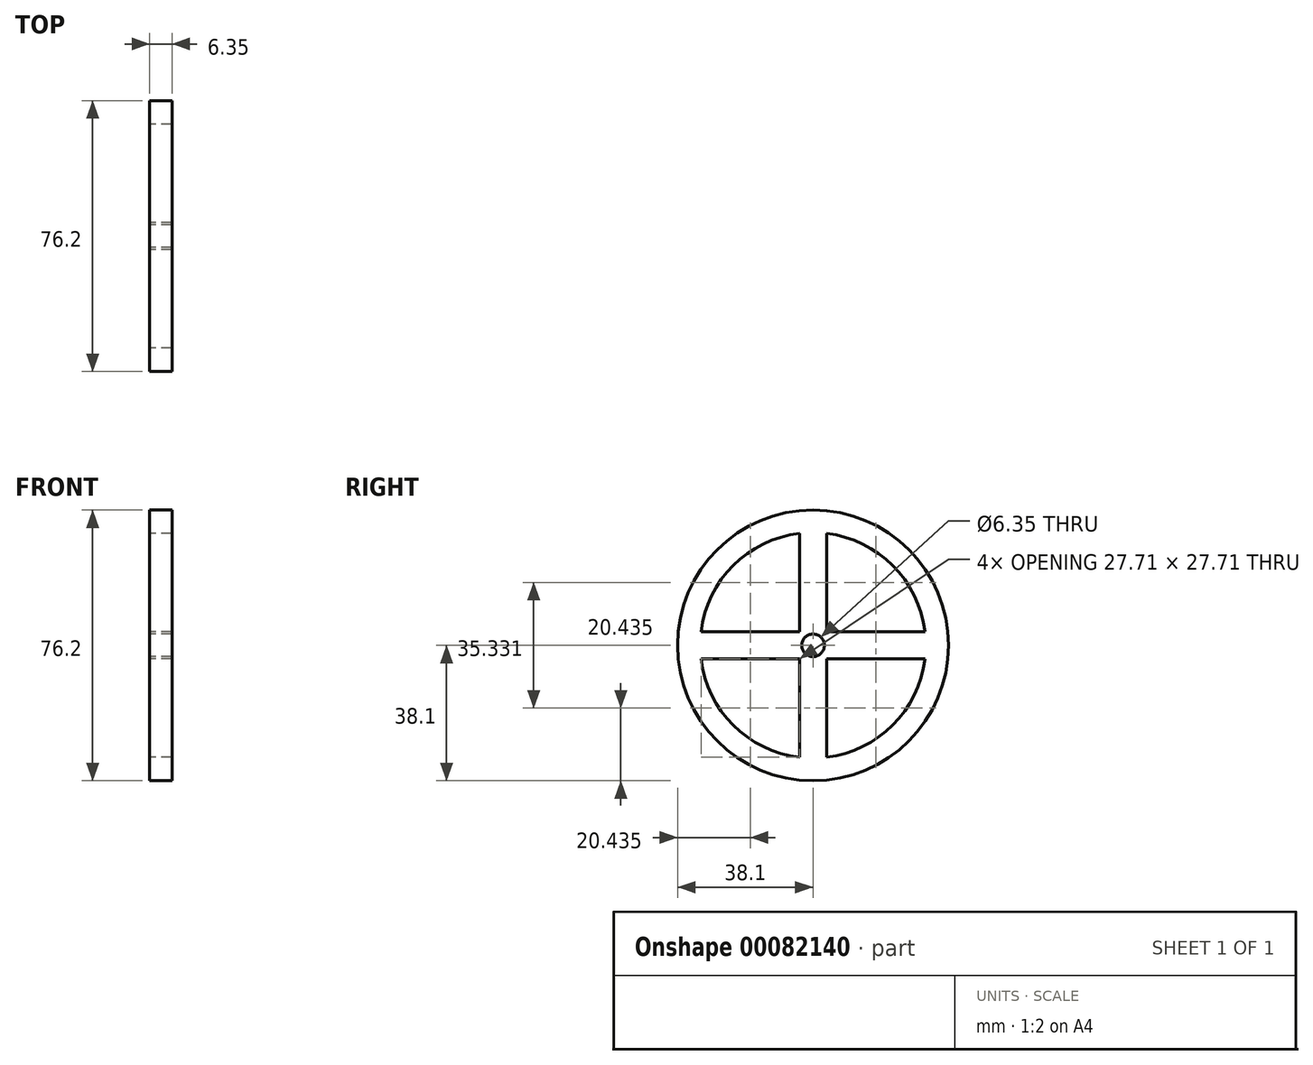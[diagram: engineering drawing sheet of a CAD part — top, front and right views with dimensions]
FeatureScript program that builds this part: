
annotation { "Feature Type Name" : "Feature", "Feature Type Description" : "" }
export const myFeature = defineFeature(function(context is Context, id is Id, definition is map)
    precondition{}
    {
        {
            var Q0;
            Q0=qCreatedBy(makeId("Right.planeOp"),FACE);
            var sketch = newSketch(context, id + "F0", { "sketchPlane" : qUnion([Q0])});
            skCircle(sketch, "E0", {"center": v(0, 0) * mm, "radius": 38.1 * mm});
            skCircle(sketch, "E1", {"center": v(0, 0) * mm, "radius": 31.75 * mm});
            skSolve(sketch);
        }
        {
            var Q0;
            Q0 = qSketchRegion(id + "F0", true);
            extrude(context, id + "F1", {"entities" : qUnion([Q0]), "depth" : 6.35 * mm});
        }
        {
            var Q0;
            Q0=qCreatedBy(makeId("Top.planeOp"),FACE);
            var sketch = newSketch(context, id + "F2", { "sketchPlane" : qUnion([Q0])});
            skLineSegment(sketch, "E2", {"start": v(0, 0) * mm, "end": v(0, -3.81) * mm});
            skLineSegment(sketch, "E3", {"start": v(0, 0) * mm, "end": v(0, 3.8) * mm});
            skLineSegment(sketch, "E4", {"start": v(0, -3.81) * mm, "end": v(6.35, -3.81) * mm});
            skLineSegment(sketch, "E5", {"start": v(0, 3.8) * mm, "end": v(6.35, 3.8) * mm});
            skLineSegment(sketch, "E6", {"start": v(6.35, -3.81) * mm, "end": v(6.35, 3.8) * mm});
            skSolve(sketch);
        }
        {
            var Q0;
            Q0 = qSketchRegion(id + "F2", true);
            extrude(context, id + "F3", {"entities" : qUnion([Q0]), "depth" : 33.02 * mm});
        }
        {
            var Q0;
            Q0=makeQuery(id+"F3.opExtrude","SWEPT_BODY",BODY,{"disambiguationData":[OSD([sQuery(id+"F2.wireOp",EDGE,"E2"),sQuery(id+"F2.wireOp",EDGE,"E3"),sQuery(id+"F2.wireOp",EDGE,"E4"),sQuery(id+"F2.wireOp",EDGE,"E5"),sQuery(id+"F2.wireOp",EDGE,"E6")])]});
            var Q1;
            Q1=makeQuery(id+"F1.opExtrude","CAP_EDGE",EDGE,{"disambiguationData":[OSD([sQuery(id+"F0.wireOp",EDGE,"E1")])],"isStart":false});
            circularPattern(context, id + "F4", {"operationType" : NewBodyOperationType.ADD, "entities" : qUnion([Q0]), "axis" : qUnion([Q1]), "angle" : 90 * degree, "instanceCount" : 4});
        }
        {
            var Q0;
            {var subQ0=makeQuery(id+"F3.opExtrude","SWEPT_FACE",FACE,{"disambiguationData":[OSD([sQuery(id+"F2.wireOp",EDGE,"E2"),sQuery(id+"F2.wireOp",EDGE,"E3")])]});Q0=makeQuery(id+"F4.boolean.opBoolean","MERGE",FACE,{"derivedFrom":[makeQuery(id+"F1.opExtrude","CAP_FACE",FACE,{"disambiguationData":[OSD([sQuery(id+"F0.wireOp",EDGE,"E0"),sQuery(id+"F0.wireOp",EDGE,"E1")])],"isStart":true}),subQ0,makeQuery(id+"F4.opPattern","COPY",FACE,{"derivedFrom":subQ0,"instanceName":"1"}),makeQuery(id+"F4.opPattern","COPY",FACE,{"derivedFrom":subQ0,"instanceName":"2"}),makeQuery(id+"F4.opPattern","COPY",FACE,{"derivedFrom":subQ0,"instanceName":"3"})]});}
            var sketch = newSketch(context, id + "F5", { "sketchPlane" : qUnion([Q0])});
            skCircle(sketch, "E7", {"center": v(0, 0) * mm, "radius": 3.18 * mm});
            skSolve(sketch);
        }
        {
            var Q0;
            Q0 = qSketchRegion(id + "F5", true);
            extrude(context, id + "F6", {"entities" : qUnion([Q0]), "operationType" : NewBodyOperationType.REMOVE, "oppositeDirection" : true, "depth" : 25.4 * mm});
        }
    });
